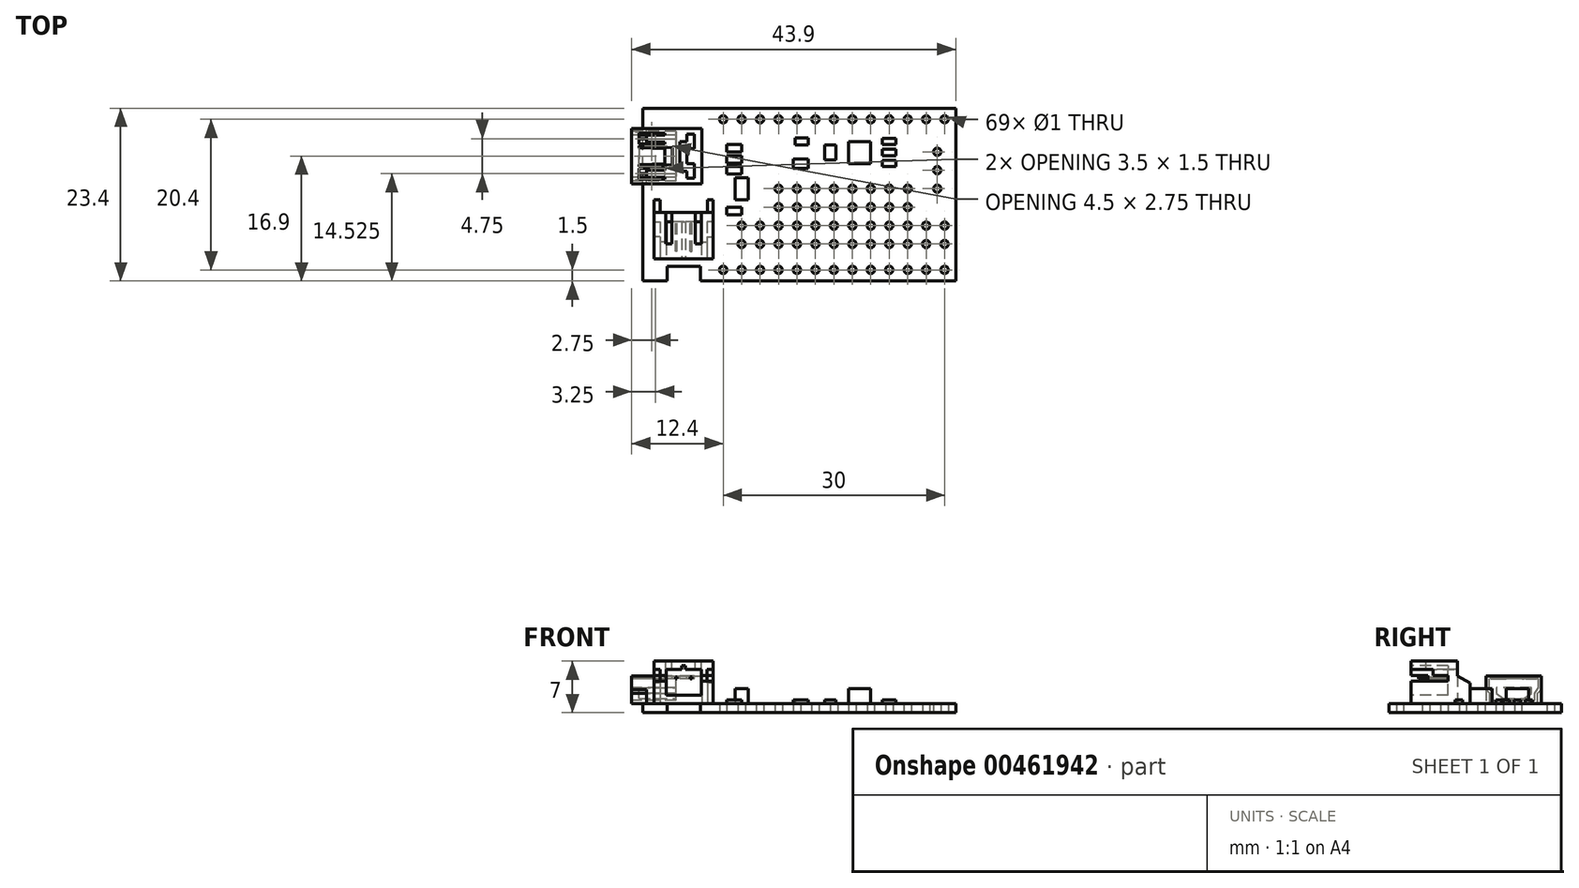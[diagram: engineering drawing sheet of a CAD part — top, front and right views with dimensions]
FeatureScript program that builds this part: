
annotation { "Feature Type Name" : "Feature", "Feature Type Description" : "" }
export const myFeature = defineFeature(function(context is Context, id is Id, definition is map)
    precondition{}
    {
        {
            var Q0;
            Q0=qCreatedBy(makeId("Top.planeOp"),FACE);
            var sketch = newSketch(context, id + "F0", { "sketchPlane" : qUnion([Q0])});
            skLineSegment(sketch, "E0.bottom", {"start": v(21.2, -11.7) * mm, "end": v(-21.2, -11.7) * mm});
            skLineSegment(sketch, "E0.top", {"start": v(21.2, 11.7) * mm, "end": v(-21.2, 11.7) * mm});
            skLineSegment(sketch, "E0.left", {"start": v(21.2, -11.7) * mm, "end": v(21.2, 11.7) * mm});
            skLineSegment(sketch, "E0.right", {"start": v(-21.2, -11.7) * mm, "end": v(-21.2, 11.7) * mm});
            skPoint(sketch, "E0.middle", {"position": v(0, 0) * mm});
            skLineSegment(sketch, "E1.bottom", {"start": v(-17.9, -11.7) * mm, "end": v(-13.4, -11.7) * mm, "construction": true});
            skLineSegment(sketch, "E1.top", {"start": v(-17.9, -9.7) * mm, "end": v(-13.4, -9.7) * mm});
            skLineSegment(sketch, "E1.left", {"start": v(-17.9, -11.7) * mm, "end": v(-17.9, -9.7) * mm});
            skLineSegment(sketch, "E1.right", {"start": v(-13.4, -11.7) * mm, "end": v(-13.4, -9.7) * mm});
            skCircle(sketch, "E2", {"center": v(19.7, -10.2) * mm, "radius": 0.5 * mm});
            skCircle(sketch, "E3.1.0.0", {"center": v(17.2, -10.2) * mm, "radius": 0.5 * mm});
            skCircle(sketch, "E3.2.0.0", {"center": v(14.7, -10.2) * mm, "radius": 0.5 * mm});
            skCircle(sketch, "E3.3.0.0", {"center": v(12.2, -10.2) * mm, "radius": 0.5 * mm});
            skCircle(sketch, "E3.4.0.0", {"center": v(9.7, -10.2) * mm, "radius": 0.5 * mm});
            skCircle(sketch, "E3.5.0.0", {"center": v(7.2, -10.2) * mm, "radius": 0.5 * mm});
            skCircle(sketch, "E3.6.0.0", {"center": v(4.7, -10.2) * mm, "radius": 0.5 * mm});
            skCircle(sketch, "E3.7.0.0", {"center": v(2.2, -10.2) * mm, "radius": 0.5 * mm});
            skCircle(sketch, "E3.8.0.0", {"center": v(-0.3, -10.2) * mm, "radius": 0.5 * mm});
            skCircle(sketch, "E3.9.0.0", {"center": v(-2.8, -10.2) * mm, "radius": 0.5 * mm});
            skCircle(sketch, "E3.10.0.0", {"center": v(-5.3, -10.2) * mm, "radius": 0.5 * mm});
            skCircle(sketch, "E3.11.0.0", {"center": v(-7.8, -10.2) * mm, "radius": 0.5 * mm});
            skCircle(sketch, "E3.12.0.0", {"center": v(-10.3, -10.2) * mm, "radius": 0.5 * mm});
            skLineSegment(sketch, "E3.direction1", {"start": v(19.7, -10.2) * mm, "end": v(17.2, -10.2) * mm, "construction": true});
            skCircle(sketch, "E4.0.1.0", {"center": v(-5.3, -6.7) * mm, "radius": 0.5 * mm});
            skCircle(sketch, "E4.0.1.1", {"center": v(-0.3, -6.7) * mm, "radius": 0.5 * mm});
            skCircle(sketch, "E4.0.1.2", {"center": v(17.2, -6.7) * mm, "radius": 0.5 * mm});
            skCircle(sketch, "E4.0.1.3", {"center": v(14.7, -6.7) * mm, "radius": 0.5 * mm});
            skCircle(sketch, "E4.0.1.4", {"center": v(12.2, -6.7) * mm, "radius": 0.5 * mm});
            skCircle(sketch, "E4.0.1.5", {"center": v(9.7, -6.7) * mm, "radius": 0.5 * mm});
            skCircle(sketch, "E4.0.1.6", {"center": v(19.7, -6.7) * mm, "radius": 0.5 * mm});
            skCircle(sketch, "E4.0.1.7", {"center": v(2.2, -6.7) * mm, "radius": 0.5 * mm});
            skCircle(sketch, "E4.0.1.8", {"center": v(4.7, -6.7) * mm, "radius": 0.5 * mm});
            skCircle(sketch, "E4.0.1.9", {"center": v(7.2, -6.7) * mm, "radius": 0.5 * mm});
            skCircle(sketch, "E4.0.1.10", {"center": v(-2.8, -6.7) * mm, "radius": 0.5 * mm});
            skCircle(sketch, "E4.0.1.12", {"center": v(-7.8, -6.7) * mm, "radius": 0.5 * mm});
            skLineSegment(sketch, "E4.direction1", {"start": v(-7.8, -10.2) * mm, "end": v(17.6, -10.2) * mm, "construction": true});
            skLineSegment(sketch, "E4.direction2", {"start": v(-7.8, -10.2) * mm, "end": v(-7.8, -6.7) * mm, "construction": true});
            skLineSegment(sketch, "E5.direction1", {"start": v(-7.8, -6.7) * mm, "end": v(17.6, -6.7) * mm, "construction": true});
            skLineSegment(sketch, "E5.direction2", {"start": v(-7.8, -6.7) * mm, "end": v(-7.8, -4.85) * mm, "construction": true});
            skPoint(sketch, "E6", {"position": v(-7.8, -8.45) * mm});
            skCircle(sketch, "E7.0.1.0", {"center": v(2.2, -4.2) * mm, "radius": 0.5 * mm});
            skCircle(sketch, "E7.0.1.1", {"center": v(9.7, -4.2) * mm, "radius": 0.5 * mm});
            skCircle(sketch, "E7.0.1.2", {"center": v(-5.3, -4.2) * mm, "radius": 0.5 * mm});
            skCircle(sketch, "E7.0.1.3", {"center": v(17.2, -4.2) * mm, "radius": 0.5 * mm});
            skCircle(sketch, "E7.0.1.4", {"center": v(-2.8, -4.2) * mm, "radius": 0.5 * mm});
            skCircle(sketch, "E7.0.1.5", {"center": v(-0.3, -4.2) * mm, "radius": 0.5 * mm});
            skCircle(sketch, "E7.0.1.6", {"center": v(14.7, -4.2) * mm, "radius": 0.5 * mm});
            skCircle(sketch, "E7.0.1.7", {"center": v(4.7, -4.2) * mm, "radius": 0.5 * mm});
            skCircle(sketch, "E7.0.1.8", {"center": v(7.2, -4.2) * mm, "radius": 0.5 * mm});
            skCircle(sketch, "E7.0.1.10", {"center": v(12.2, -4.2) * mm, "radius": 0.5 * mm});
            skCircle(sketch, "E7.0.1.11", {"center": v(19.7, -4.2) * mm, "radius": 0.5 * mm});
            skCircle(sketch, "E7.0.1.12", {"center": v(-7.8, -4.2) * mm, "radius": 0.5 * mm});
            skCircle(sketch, "E7.0.2.0", {"center": v(2.2, -1.7) * mm, "radius": 0.5 * mm});
            skCircle(sketch, "E7.0.2.1", {"center": v(9.7, -1.7) * mm, "radius": 0.5 * mm});
            skCircle(sketch, "E7.0.2.4", {"center": v(-2.8, -1.7) * mm, "radius": 0.5 * mm});
            skCircle(sketch, "E7.0.2.5", {"center": v(-0.3, -1.7) * mm, "radius": 0.5 * mm});
            skCircle(sketch, "E7.0.2.6", {"center": v(14.7, -1.7) * mm, "radius": 0.5 * mm});
            skCircle(sketch, "E7.0.2.7", {"center": v(4.7, -1.7) * mm, "radius": 0.5 * mm});
            skCircle(sketch, "E7.0.2.8", {"center": v(7.2, -1.7) * mm, "radius": 0.5 * mm});
            skCircle(sketch, "E7.0.2.10", {"center": v(12.2, -1.7) * mm, "radius": 0.5 * mm});
            skCircle(sketch, "E7.0.3.0", {"center": v(2.2, 0.8) * mm, "radius": 0.5 * mm});
            skCircle(sketch, "E7.0.3.1", {"center": v(9.7, 0.8) * mm, "radius": 0.5 * mm});
            skCircle(sketch, "E7.0.3.4", {"center": v(-2.8, 0.8) * mm, "radius": 0.5 * mm});
            skCircle(sketch, "E7.0.3.5", {"center": v(-0.3, 0.8) * mm, "radius": 0.5 * mm});
            skCircle(sketch, "E7.0.3.6", {"center": v(14.7, 0.8) * mm, "radius": 0.5 * mm});
            skCircle(sketch, "E7.0.3.7", {"center": v(4.7, 0.8) * mm, "radius": 0.5 * mm});
            skCircle(sketch, "E7.0.3.8", {"center": v(7.2, 0.8) * mm, "radius": 0.5 * mm});
            skCircle(sketch, "E7.0.3.10", {"center": v(12.2, 0.8) * mm, "radius": 0.5 * mm});
            skLineSegment(sketch, "E7.direction2", {"start": v(-7.8, -6.7) * mm, "end": v(-7.8, -4.2) * mm, "construction": true});
            skCircle(sketch, "E8", {"center": v(19.7, 10.2) * mm, "radius": 0.5 * mm});
            skCircle(sketch, "E9.1.0.0", {"center": v(17.2, 10.2) * mm, "radius": 0.5 * mm});
            skCircle(sketch, "E9.2.0.0", {"center": v(14.7, 10.2) * mm, "radius": 0.5 * mm});
            skCircle(sketch, "E9.3.0.0", {"center": v(12.2, 10.2) * mm, "radius": 0.5 * mm});
            skCircle(sketch, "E9.4.0.0", {"center": v(9.7, 10.2) * mm, "radius": 0.5 * mm});
            skCircle(sketch, "E9.5.0.0", {"center": v(7.2, 10.2) * mm, "radius": 0.5 * mm});
            skCircle(sketch, "E9.6.0.0", {"center": v(4.7, 10.2) * mm, "radius": 0.5 * mm});
            skCircle(sketch, "E9.7.0.0", {"center": v(2.2, 10.2) * mm, "radius": 0.5 * mm});
            skCircle(sketch, "E9.8.0.0", {"center": v(-0.3, 10.2) * mm, "radius": 0.5 * mm});
            skCircle(sketch, "E9.9.0.0", {"center": v(-2.8, 10.2) * mm, "radius": 0.5 * mm});
            skCircle(sketch, "E9.10.0.0", {"center": v(-5.3, 10.2) * mm, "radius": 0.5 * mm});
            skCircle(sketch, "E9.11.0.0", {"center": v(-7.8, 10.2) * mm, "radius": 0.5 * mm});
            skCircle(sketch, "E9.12.0.0", {"center": v(-10.3, 10.2) * mm, "radius": 0.5 * mm});
            skLineSegment(sketch, "E9.direction1", {"start": v(19.7, 10.2) * mm, "end": v(17.2, 10.2) * mm, "construction": true});
            skCircle(sketch, "E10", {"center": v(18.7, 0.8) * mm, "radius": 0.5 * mm});
            skCircle(sketch, "E11.0.1.0", {"center": v(18.7, 3.3) * mm, "radius": 0.5 * mm});
            skCircle(sketch, "E11.0.2.0", {"center": v(18.7, 5.8) * mm, "radius": 0.5 * mm});
            skLineSegment(sketch, "E11.direction1", {"start": v(18.7, 0.8) * mm, "end": v(43.86, 0.8) * mm, "construction": true});
            skLineSegment(sketch, "E11.direction2", {"start": v(18.7, 0.8) * mm, "end": v(18.7, 3.3) * mm, "construction": true});
            skSolve(sketch);
        }
        {
            var Q0;
            Q0=makeQuery(id+"F0.imprint","IMPRINT",FACE,{"disambiguationData":[TD([[makeQuery(id+"F0.imprint","IMPRINT",EDGE,{"derivedFrom":sQuery(id+"F0.wireOp",EDGE,"E0.top")}),1.0]])]});
            extrude(context, id + "F1", {"entities" : qUnion([Q0]), "depth" : 1.25 * mm});
        }
        {
            var Q0;
            Q0=makeQuery(id+"F1.opExtrude","CAP_FACE",FACE,{"disambiguationData":[OSD([sQuery(id+"F0.wireOp",EDGE,"E0.bottom"),sQuery(id+"F0.wireOp",EDGE,"E0.top"),sQuery(id+"F0.wireOp",EDGE,"E0.left"),sQuery(id+"F0.wireOp",EDGE,"E0.right"),sQuery(id+"F0.wireOp",EDGE,"E1.top"),sQuery(id+"F0.wireOp",EDGE,"E1.left"),sQuery(id+"F0.wireOp",EDGE,"E1.right"),sQuery(id+"F0.wireOp",EDGE,"E2"),sQuery(id+"F0.wireOp",EDGE,"E3.1.0.0"),sQuery(id+"F0.wireOp",EDGE,"E3.2.0.0"),sQuery(id+"F0.wireOp",EDGE,"E3.3.0.0"),sQuery(id+"F0.wireOp",EDGE,"E3.4.0.0"),sQuery(id+"F0.wireOp",EDGE,"E3.5.0.0"),sQuery(id+"F0.wireOp",EDGE,"E3.6.0.0"),sQuery(id+"F0.wireOp",EDGE,"E3.7.0.0"),sQuery(id+"F0.wireOp",EDGE,"E3.8.0.0"),sQuery(id+"F0.wireOp",EDGE,"E3.9.0.0"),sQuery(id+"F0.wireOp",EDGE,"E3.10.0.0"),sQuery(id+"F0.wireOp",EDGE,"E3.11.0.0"),sQuery(id+"F0.wireOp",EDGE,"E3.12.0.0"),sQuery(id+"F0.wireOp",EDGE,"E4.0.1.0"),sQuery(id+"F0.wireOp",EDGE,"E4.0.1.1"),sQuery(id+"F0.wireOp",EDGE,"E4.0.1.2"),sQuery(id+"F0.wireOp",EDGE,"E4.0.1.3"),sQuery(id+"F0.wireOp",EDGE,"E4.0.1.4"),sQuery(id+"F0.wireOp",EDGE,"E4.0.1.5"),sQuery(id+"F0.wireOp",EDGE,"E4.0.1.6"),sQuery(id+"F0.wireOp",EDGE,"E4.0.1.7"),sQuery(id+"F0.wireOp",EDGE,"E4.0.1.8"),sQuery(id+"F0.wireOp",EDGE,"E4.0.1.9"),sQuery(id+"F0.wireOp",EDGE,"E4.0.1.10"),sQuery(id+"F0.wireOp",EDGE,"E4.0.1.12"),sQuery(id+"F0.wireOp",EDGE,"E7.0.1.0"),sQuery(id+"F0.wireOp",EDGE,"E7.0.1.1"),sQuery(id+"F0.wireOp",EDGE,"E7.0.1.2"),sQuery(id+"F0.wireOp",EDGE,"E7.0.1.3"),sQuery(id+"F0.wireOp",EDGE,"E7.0.1.4"),sQuery(id+"F0.wireOp",EDGE,"E7.0.1.5"),sQuery(id+"F0.wireOp",EDGE,"E7.0.1.6"),sQuery(id+"F0.wireOp",EDGE,"E7.0.1.7"),sQuery(id+"F0.wireOp",EDGE,"E7.0.1.8"),sQuery(id+"F0.wireOp",EDGE,"E7.0.1.10"),sQuery(id+"F0.wireOp",EDGE,"E7.0.1.11"),sQuery(id+"F0.wireOp",EDGE,"E7.0.1.12"),sQuery(id+"F0.wireOp",EDGE,"E7.0.2.0"),sQuery(id+"F0.wireOp",EDGE,"E7.0.2.1"),sQuery(id+"F0.wireOp",EDGE,"E7.0.2.4"),sQuery(id+"F0.wireOp",EDGE,"E7.0.2.5"),sQuery(id+"F0.wireOp",EDGE,"E7.0.2.6"),sQuery(id+"F0.wireOp",EDGE,"E7.0.2.7"),sQuery(id+"F0.wireOp",EDGE,"E7.0.2.8"),sQuery(id+"F0.wireOp",EDGE,"E7.0.2.10"),sQuery(id+"F0.wireOp",EDGE,"E7.0.3.0"),sQuery(id+"F0.wireOp",EDGE,"E7.0.3.1"),sQuery(id+"F0.wireOp",EDGE,"E7.0.3.4"),sQuery(id+"F0.wireOp",EDGE,"E7.0.3.5"),sQuery(id+"F0.wireOp",EDGE,"E7.0.3.6"),sQuery(id+"F0.wireOp",EDGE,"E7.0.3.7"),sQuery(id+"F0.wireOp",EDGE,"E7.0.3.8"),sQuery(id+"F0.wireOp",EDGE,"E7.0.3.10"),sQuery(id+"F0.wireOp",EDGE,"E8"),sQuery(id+"F0.wireOp",EDGE,"E9.1.0.0"),sQuery(id+"F0.wireOp",EDGE,"E9.2.0.0"),sQuery(id+"F0.wireOp",EDGE,"E9.3.0.0"),sQuery(id+"F0.wireOp",EDGE,"E9.4.0.0"),sQuery(id+"F0.wireOp",EDGE,"E9.5.0.0"),sQuery(id+"F0.wireOp",EDGE,"E9.6.0.0"),sQuery(id+"F0.wireOp",EDGE,"E9.7.0.0"),sQuery(id+"F0.wireOp",EDGE,"E9.8.0.0"),sQuery(id+"F0.wireOp",EDGE,"E9.9.0.0"),sQuery(id+"F0.wireOp",EDGE,"E9.10.0.0"),sQuery(id+"F0.wireOp",EDGE,"E9.11.0.0"),sQuery(id+"F0.wireOp",EDGE,"E9.12.0.0"),sQuery(id+"F0.wireOp",EDGE,"E10"),sQuery(id+"F0.wireOp",EDGE,"E11.0.1.0"),sQuery(id+"F0.wireOp",EDGE,"E11.0.2.0")])],"isStart":false});
            var sketch = newSketch(context, id + "F2", { "sketchPlane" : qUnion([Q0])});
            skCircle(sketch, "E12", {"center": v(12.2, 10.2) * mm, "radius": 0.5 * mm});
            skCircle(sketch, "E13", {"center": v(-7.8, 10.2) * mm, "radius": 0.5 * mm});
            skCircle(sketch, "E14", {"center": v(-2.8, 0.8) * mm, "radius": 0.5 * mm});
            skSolve(sketch);
        }
        {
            var Q0;
            Q0=makeQuery(id+"F1.opExtrude","CAP_FACE",FACE,{"disambiguationData":[OSD([sQuery(id+"F0.wireOp",EDGE,"E0.bottom"),sQuery(id+"F0.wireOp",EDGE,"E0.top"),sQuery(id+"F0.wireOp",EDGE,"E0.left"),sQuery(id+"F0.wireOp",EDGE,"E0.right"),sQuery(id+"F0.wireOp",EDGE,"E1.top"),sQuery(id+"F0.wireOp",EDGE,"E1.left"),sQuery(id+"F0.wireOp",EDGE,"E1.right"),sQuery(id+"F0.wireOp",EDGE,"E2"),sQuery(id+"F0.wireOp",EDGE,"E3.1.0.0"),sQuery(id+"F0.wireOp",EDGE,"E3.2.0.0"),sQuery(id+"F0.wireOp",EDGE,"E3.3.0.0"),sQuery(id+"F0.wireOp",EDGE,"E3.4.0.0"),sQuery(id+"F0.wireOp",EDGE,"E3.5.0.0"),sQuery(id+"F0.wireOp",EDGE,"E3.6.0.0"),sQuery(id+"F0.wireOp",EDGE,"E3.7.0.0"),sQuery(id+"F0.wireOp",EDGE,"E3.8.0.0"),sQuery(id+"F0.wireOp",EDGE,"E3.9.0.0"),sQuery(id+"F0.wireOp",EDGE,"E3.10.0.0"),sQuery(id+"F0.wireOp",EDGE,"E3.11.0.0"),sQuery(id+"F0.wireOp",EDGE,"E3.12.0.0"),sQuery(id+"F0.wireOp",EDGE,"E4.0.1.0"),sQuery(id+"F0.wireOp",EDGE,"E4.0.1.1"),sQuery(id+"F0.wireOp",EDGE,"E4.0.1.2"),sQuery(id+"F0.wireOp",EDGE,"E4.0.1.3"),sQuery(id+"F0.wireOp",EDGE,"E4.0.1.4"),sQuery(id+"F0.wireOp",EDGE,"E4.0.1.5"),sQuery(id+"F0.wireOp",EDGE,"E4.0.1.6"),sQuery(id+"F0.wireOp",EDGE,"E4.0.1.7"),sQuery(id+"F0.wireOp",EDGE,"E4.0.1.8"),sQuery(id+"F0.wireOp",EDGE,"E4.0.1.9"),sQuery(id+"F0.wireOp",EDGE,"E4.0.1.10"),sQuery(id+"F0.wireOp",EDGE,"E4.0.1.12"),sQuery(id+"F0.wireOp",EDGE,"E7.0.1.0"),sQuery(id+"F0.wireOp",EDGE,"E7.0.1.1"),sQuery(id+"F0.wireOp",EDGE,"E7.0.1.2"),sQuery(id+"F0.wireOp",EDGE,"E7.0.1.3"),sQuery(id+"F0.wireOp",EDGE,"E7.0.1.4"),sQuery(id+"F0.wireOp",EDGE,"E7.0.1.5"),sQuery(id+"F0.wireOp",EDGE,"E7.0.1.6"),sQuery(id+"F0.wireOp",EDGE,"E7.0.1.7"),sQuery(id+"F0.wireOp",EDGE,"E7.0.1.8"),sQuery(id+"F0.wireOp",EDGE,"E7.0.1.10"),sQuery(id+"F0.wireOp",EDGE,"E7.0.1.11"),sQuery(id+"F0.wireOp",EDGE,"E7.0.1.12"),sQuery(id+"F0.wireOp",EDGE,"E7.0.2.0"),sQuery(id+"F0.wireOp",EDGE,"E7.0.2.1"),sQuery(id+"F0.wireOp",EDGE,"E7.0.2.4"),sQuery(id+"F0.wireOp",EDGE,"E7.0.2.5"),sQuery(id+"F0.wireOp",EDGE,"E7.0.2.6"),sQuery(id+"F0.wireOp",EDGE,"E7.0.2.7"),sQuery(id+"F0.wireOp",EDGE,"E7.0.2.8"),sQuery(id+"F0.wireOp",EDGE,"E7.0.2.10"),sQuery(id+"F0.wireOp",EDGE,"E7.0.3.0"),sQuery(id+"F0.wireOp",EDGE,"E7.0.3.1"),sQuery(id+"F0.wireOp",EDGE,"E7.0.3.4"),sQuery(id+"F0.wireOp",EDGE,"E7.0.3.5"),sQuery(id+"F0.wireOp",EDGE,"E7.0.3.6"),sQuery(id+"F0.wireOp",EDGE,"E7.0.3.7"),sQuery(id+"F0.wireOp",EDGE,"E7.0.3.8"),sQuery(id+"F0.wireOp",EDGE,"E7.0.3.10"),sQuery(id+"F0.wireOp",EDGE,"E8"),sQuery(id+"F0.wireOp",EDGE,"E9.1.0.0"),sQuery(id+"F0.wireOp",EDGE,"E9.2.0.0"),sQuery(id+"F0.wireOp",EDGE,"E9.3.0.0"),sQuery(id+"F0.wireOp",EDGE,"E9.4.0.0"),sQuery(id+"F0.wireOp",EDGE,"E9.5.0.0"),sQuery(id+"F0.wireOp",EDGE,"E9.6.0.0"),sQuery(id+"F0.wireOp",EDGE,"E9.7.0.0"),sQuery(id+"F0.wireOp",EDGE,"E9.8.0.0"),sQuery(id+"F0.wireOp",EDGE,"E9.9.0.0"),sQuery(id+"F0.wireOp",EDGE,"E9.10.0.0"),sQuery(id+"F0.wireOp",EDGE,"E9.11.0.0"),sQuery(id+"F0.wireOp",EDGE,"E9.12.0.0"),sQuery(id+"F0.wireOp",EDGE,"E10"),sQuery(id+"F0.wireOp",EDGE,"E11.0.1.0"),sQuery(id+"F0.wireOp",EDGE,"E11.0.2.0")])],"isStart":false});
            var sketch = newSketch(context, id + "F3", { "sketchPlane" : qUnion([Q0])});
            skLineSegment(sketch, "E15.bottom", {"start": v(13.13, 3.77) * mm, "end": v(11.28, 3.77) * mm});
            skLineSegment(sketch, "E15.top", {"start": v(13.13, 4.62) * mm, "end": v(11.28, 4.62) * mm});
            skLineSegment(sketch, "E15.left", {"start": v(13.13, 3.77) * mm, "end": v(13.12, 4.62) * mm});
            skLineSegment(sketch, "E15.right", {"start": v(11.28, 3.77) * mm, "end": v(11.28, 4.62) * mm});
            skPoint(sketch, "E15.middle", {"position": v(12.2, 4.2) * mm});
            skPoint(sketch, "E16.0.1.0", {"position": v(12.2, 5.7) * mm});
            skLineSegment(sketch, "E16.0.1.1", {"start": v(13.12, 5.27) * mm, "end": v(11.28, 5.27) * mm});
            skLineSegment(sketch, "E16.0.1.2", {"start": v(13.12, 6.12) * mm, "end": v(11.28, 6.12) * mm});
            skLineSegment(sketch, "E16.0.1.3", {"start": v(13.12, 5.27) * mm, "end": v(13.12, 6.12) * mm});
            skLineSegment(sketch, "E16.0.1.4", {"start": v(11.27, 5.27) * mm, "end": v(11.27, 6.12) * mm});
            skPoint(sketch, "E16.0.2.0", {"position": v(12.2, 7.2) * mm});
            skLineSegment(sketch, "E16.0.2.1", {"start": v(13.13, 6.77) * mm, "end": v(11.28, 6.77) * mm});
            skLineSegment(sketch, "E16.0.2.2", {"start": v(13.13, 7.62) * mm, "end": v(11.28, 7.62) * mm});
            skLineSegment(sketch, "E16.0.2.3", {"start": v(13.12, 6.77) * mm, "end": v(13.12, 7.62) * mm});
            skLineSegment(sketch, "E16.0.2.4", {"start": v(11.27, 6.77) * mm, "end": v(11.27, 7.62) * mm});
            skLineSegment(sketch, "E16.direction1", {"start": v(11.28, 3.77) * mm, "end": v(37.64, 3.77) * mm, "construction": true});
            skLineSegment(sketch, "E16.direction2", {"start": v(11.28, 3.77) * mm, "end": v(11.28, 5.27) * mm, "construction": true});
            skSolve(sketch);
        }
        {
            var Q0;
            Q0=makeQuery(id+"F2.imprint","IMPRINT",FACE,{"disambiguationData":[TD([[makeQuery(id+"F2.imprint","IMPRINT",EDGE,{"derivedFrom":sQuery(id+"F2.wireOp",EDGE,"E12")}),-1.0]])]});
            var sketch = newSketch(context, id + "F4", { "sketchPlane" : qUnion([Q0])});
            skLineSegment(sketch, "E17.bottom", {"start": v(9.7, 4.2) * mm, "end": v(6.7, 4.2) * mm});
            skLineSegment(sketch, "E17.top", {"start": v(9.7, 7.2) * mm, "end": v(6.7, 7.2) * mm});
            skLineSegment(sketch, "E17.left", {"start": v(9.7, 4.2) * mm, "end": v(9.7, 7.2) * mm});
            skLineSegment(sketch, "E17.right", {"start": v(6.7, 4.2) * mm, "end": v(6.7, 7.2) * mm});
            skPoint(sketch, "E17.middle", {"position": v(8.2, 5.7) * mm});
            skSolve(sketch);
        }
        {
            var Q0;
            Q0=makeQuery(id+"F2.imprint","IMPRINT",FACE,{"disambiguationData":[TD([[makeQuery(id+"F2.imprint","IMPRINT",EDGE,{"derivedFrom":sQuery(id+"F2.wireOp",EDGE,"E12")}),-1.0]])]});
            var sketch = newSketch(context, id + "F5", { "sketchPlane" : qUnion([Q0])});
            skLineSegment(sketch, "E18.bottom", {"start": v(4.95, 4.7) * mm, "end": v(3.45, 4.7) * mm});
            skLineSegment(sketch, "E18.top", {"start": v(4.95, 6.7) * mm, "end": v(3.45, 6.7) * mm});
            skLineSegment(sketch, "E18.left", {"start": v(4.95, 4.7) * mm, "end": v(4.95, 6.7) * mm});
            skLineSegment(sketch, "E18.right", {"start": v(3.45, 4.7) * mm, "end": v(3.45, 6.7) * mm});
            skPoint(sketch, "E18.middle", {"position": v(4.2, 5.7) * mm});
            skSolve(sketch);
        }
        {
            var Q0;
            Q0=makeQuery(id+"F2.imprint","IMPRINT",FACE,{"disambiguationData":[TD([[makeQuery(id+"F2.imprint","IMPRINT",EDGE,{"derivedFrom":sQuery(id+"F2.wireOp",EDGE,"E12")}),-1.0]])]});
            var sketch = newSketch(context, id + "F6", { "sketchPlane" : qUnion([Q0])});
            skLineSegment(sketch, "E19.bottom", {"start": v(1.2, 6.7) * mm, "end": v(-0.55, 6.7) * mm});
            skLineSegment(sketch, "E19.top", {"start": v(1.2, 7.7) * mm, "end": v(-0.55, 7.7) * mm});
            skLineSegment(sketch, "E19.left", {"start": v(1.2, 6.7) * mm, "end": v(1.2, 7.7) * mm});
            skLineSegment(sketch, "E19.right", {"start": v(-0.55, 6.7) * mm, "end": v(-0.55, 7.7) * mm});
            skPoint(sketch, "E19.middle", {"position": v(0.32, 7.2) * mm});
            skLineSegment(sketch, "E20.bottom", {"start": v(1.2, 3.57) * mm, "end": v(-0.8, 3.57) * mm});
            skLineSegment(sketch, "E20.top", {"start": v(1.2, 4.82) * mm, "end": v(-0.8, 4.82) * mm});
            skLineSegment(sketch, "E20.left", {"start": v(1.2, 3.57) * mm, "end": v(1.2, 4.82) * mm});
            skLineSegment(sketch, "E20.right", {"start": v(-0.8, 3.57) * mm, "end": v(-0.8, 4.82) * mm});
            skPoint(sketch, "E20.middle", {"position": v(0.2, 4.2) * mm});
            skSolve(sketch);
        }
        {
            var Q0;
            Q0=makeQuery(id+"F2.imprint","IMPRINT",FACE,{"disambiguationData":[TD([[makeQuery(id+"F2.imprint","IMPRINT",EDGE,{"derivedFrom":sQuery(id+"F2.wireOp",EDGE,"E12")}),-1.0]])]});
            var sketch = newSketch(context, id + "F7", { "sketchPlane" : qUnion([Q0])});
            skLineSegment(sketch, "E21.bottom", {"start": v(-7.8, 5.77) * mm, "end": v(-9.8, 5.77) * mm});
            skLineSegment(sketch, "E21.top", {"start": v(-7.8, 6.77) * mm, "end": v(-9.8, 6.77) * mm});
            skLineSegment(sketch, "E21.left", {"start": v(-7.8, 5.77) * mm, "end": v(-7.8, 6.77) * mm});
            skLineSegment(sketch, "E21.right", {"start": v(-9.8, 5.77) * mm, "end": v(-9.8, 6.77) * mm});
            skPoint(sketch, "E21.middle", {"position": v(-8.8, 6.27) * mm});
            skLineSegment(sketch, "E22.0.1.0", {"start": v(-7.8, 4.27) * mm, "end": v(-7.8, 5.27) * mm});
            skLineSegment(sketch, "E22.0.1.1", {"start": v(-9.8, 4.27) * mm, "end": v(-9.8, 5.27) * mm});
            skLineSegment(sketch, "E22.0.1.2", {"start": v(-7.8, 4.27) * mm, "end": v(-9.8, 4.27) * mm});
            skLineSegment(sketch, "E22.0.1.3", {"start": v(-7.8, 5.27) * mm, "end": v(-9.8, 5.27) * mm});
            skPoint(sketch, "E22.0.1.4", {"position": v(-8.8, 4.77) * mm});
            skLineSegment(sketch, "E22.0.2.0", {"start": v(-7.8, 2.77) * mm, "end": v(-7.8, 3.77) * mm});
            skLineSegment(sketch, "E22.0.2.1", {"start": v(-9.8, 2.77) * mm, "end": v(-9.8, 3.77) * mm});
            skLineSegment(sketch, "E22.0.2.2", {"start": v(-7.8, 2.77) * mm, "end": v(-9.8, 2.77) * mm});
            skLineSegment(sketch, "E22.0.2.3", {"start": v(-7.8, 3.77) * mm, "end": v(-9.8, 3.77) * mm});
            skPoint(sketch, "E22.0.2.4", {"position": v(-8.8, 3.27) * mm});
            skLineSegment(sketch, "E22.direction1", {"start": v(-9.8, 5.77) * mm, "end": v(16.86, 5.77) * mm, "construction": true});
            skLineSegment(sketch, "E22.direction2", {"start": v(-9.8, 5.77) * mm, "end": v(-9.8, 4.27) * mm, "construction": true});
            skLineSegment(sketch, "E23.direction1", {"start": v(-9.8, 2.77) * mm, "end": v(15.6, 2.77) * mm, "construction": true});
            skPoint(sketch, "E24.0.1.0", {"position": v(-8.8, -2.23) * mm});
            skLineSegment(sketch, "E24.0.1.1", {"start": v(-9.8, -2.73) * mm, "end": v(-9.8, -1.73) * mm});
            skLineSegment(sketch, "E24.0.1.2", {"start": v(-7.8, -2.73) * mm, "end": v(-7.8, -1.73) * mm});
            skLineSegment(sketch, "E24.0.1.3", {"start": v(-7.8, -1.73) * mm, "end": v(-9.8, -1.73) * mm});
            skLineSegment(sketch, "E24.0.1.4", {"start": v(-7.8, -2.73) * mm, "end": v(-9.8, -2.73) * mm});
            skLineSegment(sketch, "E24.direction2", {"start": v(-9.8, 2.77) * mm, "end": v(-9.8, -2.73) * mm, "construction": true});
            skSolve(sketch);
        }
        {
            var Q0;
            Q0=makeQuery(id+"F2.imprint","IMPRINT",FACE,{"disambiguationData":[TD([[makeQuery(id+"F2.imprint","IMPRINT",EDGE,{"derivedFrom":sQuery(id+"F2.wireOp",EDGE,"E12")}),-1.0]])]});
            var sketch = newSketch(context, id + "F8", { "sketchPlane" : qUnion([Q0])});
            skLineSegment(sketch, "E25.bottom", {"start": v(-6.93, -0.7) * mm, "end": v(-8.68, -0.7) * mm});
            skLineSegment(sketch, "E25.top", {"start": v(-6.93, 2.3) * mm, "end": v(-8.68, 2.3) * mm});
            skLineSegment(sketch, "E25.left", {"start": v(-6.93, -0.7) * mm, "end": v(-6.93, 2.3) * mm});
            skLineSegment(sketch, "E25.right", {"start": v(-8.68, -0.7) * mm, "end": v(-8.68, 2.3) * mm});
            skPoint(sketch, "E25.middle", {"position": v(-7.8, 0.8) * mm});
            skSolve(sketch);
        }
        {
            var Q0;
            Q0 = qSketchRegion(id + "F3", true);
            extrude(context, id + "F9", {"entities" : qUnion([Q0]), "depth" : .5 * mm});
        }
        {
            var Q0;
            Q0 = qSketchRegion(id + "F5", true);
            extrude(context, id + "F10", {"entities" : qUnion([Q0]), "depth" : .5 * mm});
        }
        {
            var Q0;
            Q0 = qSketchRegion(id + "F6", true);
            extrude(context, id + "F11", {"entities" : qUnion([Q0]), "depth" : .5 * mm});
        }
        {
            var Q0;
            Q0 = qSketchRegion(id + "F7", true);
            extrude(context, id + "F12", {"entities" : qUnion([Q0]), "depth" : .5 * mm});
        }
        {
            var Q0;
            Q0 = qSketchRegion(id + "F4", true);
            extrude(context, id + "F13", {"entities" : qUnion([Q0]), "depth" : 2 * mm});
        }
        {
            var Q0;
            Q0 = qSketchRegion(id + "F8", true);
            extrude(context, id + "F14", {"entities" : qUnion([Q0]), "depth" : 2 * mm});
        }
        {
            var Q0;
            Q0=makeQuery(id+"F2.imprint","IMPRINT",FACE,{"disambiguationData":[TD([[makeQuery(id+"F2.imprint","IMPRINT",EDGE,{"derivedFrom":sQuery(id+"F2.wireOp",EDGE,"E12")}),-1.0]])]});
            var sketch = newSketch(context, id + "F15", { "sketchPlane" : qUnion([Q0])});
            skLineSegment(sketch, "E26.bottom", {"start": v(-11.65, -8.7) * mm, "end": v(-19.65, -8.7) * mm});
            skLineSegment(sketch, "E26.top", {"start": v(-11.65, -0.7) * mm, "end": v(-19.65, -0.7) * mm});
            skLineSegment(sketch, "E26.left", {"start": v(-11.65, -8.7) * mm, "end": v(-11.65, -0.7) * mm});
            skLineSegment(sketch, "E26.right", {"start": v(-19.65, -8.7) * mm, "end": v(-19.65, -0.7) * mm});
            skPoint(sketch, "E26.middle", {"position": v(-15.65, -4.7) * mm});
            skLineSegment(sketch, "E27.bottom", {"start": v(-18.85, -0.7) * mm, "end": v(-12.45, -0.7) * mm});
            skLineSegment(sketch, "E27.top", {"start": v(-18.85, -2.45) * mm, "end": v(-12.45, -2.45) * mm});
            skLineSegment(sketch, "E27.left", {"start": v(-18.85, -0.7) * mm, "end": v(-18.85, -2.45) * mm});
            skLineSegment(sketch, "E27.right", {"start": v(-12.45, -0.7) * mm, "end": v(-12.45, -2.45) * mm});
            skPoint(sketch, "E28", {"position": v(-15.65, -2.45) * mm});
            skSolve(sketch);
        }
        {
            var Q0;
            Q0=makeQuery(id+"F15.imprint","IMPRINT",FACE,{"disambiguationData":[TD([[makeQuery(id+"F15.imprint","IMPRINT",EDGE,{"derivedFrom":sQuery(id+"F15.wireOp",EDGE,"E26.bottom")}),-1.0]])]});
            extrude(context, id + "F16", {"entities" : qUnion([Q0]), "depth" : 5.75 * mm});
        }
        {
            var Q0;
            Q0=makeQuery(id+"F2.imprint","IMPRINT",FACE,{"disambiguationData":[TD([[makeQuery(id+"F2.imprint","IMPRINT",EDGE,{"derivedFrom":sQuery(id+"F2.wireOp",EDGE,"E12")}),-1.0]])]});
            var sketch = newSketch(context, id + "F17", { "sketchPlane" : qUnion([Q0])});
            skLineSegment(sketch, "E29.bottom", {"start": v(-22.7, 1.45) * mm, "end": v(-13.2, 1.45) * mm});
            skLineSegment(sketch, "E29.top", {"start": v(-22.7, 8.95) * mm, "end": v(-13.2, 8.95) * mm});
            skLineSegment(sketch, "E29.left", {"start": v(-22.7, 1.45) * mm, "end": v(-22.7, 8.95) * mm});
            skLineSegment(sketch, "E29.right", {"start": v(-13.2, 1.45) * mm, "end": v(-13.2, 8.95) * mm});
            skPoint(sketch, "E29.middle", {"position": v(-17.95, 5.2) * mm});
            skSolve(sketch);
        }
        {
            var Q0;
            Q0 = qSketchRegion(id + "F17", true);
            extrude(context, id + "F18", {"entities" : qUnion([Q0]), "depth" : 3.75 * mm});
        }
        {
            var Q0;
            Q0=makeQuery(id+"F16.opExtrude","SWEPT_FACE",FACE,{"disambiguationData":[OSD([sQuery(id+"F15.wireOp",EDGE,"E26.bottom")])]});
            var sketch = newSketch(context, id + "F19", { "sketchPlane" : qUnion([Q0])});
            skLineSegment(sketch, "E30.bottom", {"start": v(-13.28, 2.37) * mm, "end": v(-18.03, 2.37) * mm});
            skLineSegment(sketch, "E30.top", {"start": v(-13.28, 5.87) * mm, "end": v(-18.03, 5.87) * mm});
            skLineSegment(sketch, "E30.left", {"start": v(-13.28, 2.37) * mm, "end": v(-13.28, 5.87) * mm});
            skLineSegment(sketch, "E30.right", {"start": v(-18.03, 2.37) * mm, "end": v(-18.03, 5.88) * mm});
            skPoint(sketch, "E30.middle", {"position": v(-15.65, 4.12) * mm});
            skSolve(sketch);
        }
        {
            var Q0;
            Q0=makeQuery(id+"F19.imprint","IMPRINT",FACE,{"disambiguationData":[TD([[makeQuery(id+"F19.imprint","IMPRINT",EDGE,{"derivedFrom":sQuery(id+"F19.wireOp",EDGE,"E30.bottom")}),-1.0]])]});
            extrude(context, id + "F20", {"entities" : qUnion([Q0]), "operationType" : NewBodyOperationType.REMOVE, "oppositeDirection" : true, "depth" : 5 * mm});
        }
        {
            var Q0;
            Q0=makeQuery(id+"F18.opExtrude","SWEPT_FACE",FACE,{"disambiguationData":[OSD([sQuery(id+"F17.wireOp",EDGE,"E29.left")])]});
            var sketch = newSketch(context, id + "F21", { "sketchPlane" : qUnion([Q0])});
            skLineSegment(sketch, "E31.bottom", {"start": v(-1.95, 1.25) * mm, "end": v(-8.45, 1.25) * mm});
            skLineSegment(sketch, "E31.top", {"start": v(-1.95, 2.62) * mm, "end": v(-8.45, 2.62) * mm});
            skLineSegment(sketch, "E31.left", {"start": v(-1.95, 1.25) * mm, "end": v(-1.95, 2.62) * mm});
            skLineSegment(sketch, "E31.right", {"start": v(-8.45, 1.25) * mm, "end": v(-8.45, 2.62) * mm});
            skPoint(sketch, "E31.middle", {"position": v(-5.2, 1.94) * mm});
            skLineSegment(sketch, "E32", {"start": v(-8.45, 2.62) * mm, "end": v(-8.95, 3.13) * mm});
            skLineSegment(sketch, "E33", {"start": v(-1.45, 3.12) * mm, "end": v(-1.95, 2.62) * mm});
            skSolve(sketch);
        }
        {
            var Q0;
            {var subQ0=sQuery(id+"F21.wireOp",EDGE,"E31.right");Q0=makeQuery(id+"F21.imprint","IMPRINT",FACE,{"disambiguationData":[TD([[makeQuery(id+"F21.imprint","IMPRINT",EDGE,{"derivedFrom":subQ0}),1.0]])]});}
            var Q1;
            {var subQ0=sQuery(id+"F21.wireOp",EDGE,"E31.left");Q1=makeQuery(id+"F21.imprint","IMPRINT",FACE,{"disambiguationData":[TD([[makeQuery(id+"F21.imprint","IMPRINT",EDGE,{"derivedFrom":subQ0}),-1.0]])]});}
            extrude(context, id + "F22", {"entities" : qUnion([Q0, Q1]), "operationType" : NewBodyOperationType.REMOVE, "oppositeDirection" : true, "depth" : 2 * mm});
        }
        {
            var Q0;
            Q0=makeQuery(id+"F18.opExtrude","SWEPT_FACE",FACE,{"disambiguationData":[OSD([sQuery(id+"F17.wireOp",EDGE,"E29.left")])]});
            var sketch = newSketch(context, id + "F23", { "sketchPlane" : qUnion([Q0])});
            skLineSegment(sketch, "E34", {"start": v(-8.55, 4.6) * mm, "end": v(-1.85, 4.6) * mm});
            skLineSegment(sketch, "E35", {"start": v(-1.85, 4.6) * mm, "end": v(-1.85, 3.37) * mm});
            skLineSegment(sketch, "E36", {"start": v(-1.85, 3.37) * mm, "end": v(-2.35, 2.62) * mm});
            skLineSegment(sketch, "E37", {"start": v(-2.35, 2.62) * mm, "end": v(-2.35, 1.65) * mm});
            skLineSegment(sketch, "E38", {"start": v(-2.35, 1.65) * mm, "end": v(-8.05, 1.65) * mm});
            skLineSegment(sketch, "E39", {"start": v(-8.05, 1.65) * mm, "end": v(-8.05, 2.62) * mm});
            skLineSegment(sketch, "E40", {"start": v(-8.05, 2.62) * mm, "end": v(-8.55, 3.37) * mm});
            skLineSegment(sketch, "E41", {"start": v(-8.55, 3.37) * mm, "end": v(-8.55, 4.6) * mm});
            skPoint(sketch, "E42", {"position": v(-5.2, 4.6) * mm});
            skPoint(sketch, "E43", {"position": v(-5.2, 1.65) * mm});
            skSolve(sketch);
        }
        {
            var Q0;
            Q0=makeQuery(id+"F23.imprint","IMPRINT",FACE,{"disambiguationData":[TD([[makeQuery(id+"F23.imprint","IMPRINT",EDGE,{"derivedFrom":sQuery(id+"F23.wireOp",EDGE,"E34")}),-1.0]])]});
            extrude(context, id + "F24", {"entities" : qUnion([Q0]), "operationType" : NewBodyOperationType.REMOVE, "oppositeDirection" : true, "depth" : 6 * mm});
        }
        {
            var Q0;
            Q0=makeQuery(id+"F18.opExtrude","CAP_FACE",FACE,{"disambiguationData":[OSD([sQuery(id+"F17.wireOp",EDGE,"E29.bottom"),sQuery(id+"F17.wireOp",EDGE,"E29.top"),sQuery(id+"F17.wireOp",EDGE,"E29.left"),sQuery(id+"F17.wireOp",EDGE,"E29.right")])],"isStart":false});
            var sketch = newSketch(context, id + "F25", { "sketchPlane" : qUnion([Q0])});
            skLineSegment(sketch, "E44", {"start": v(-13.2, 5.2) * mm, "end": v(-22.7, 5.2) * mm, "construction": true});
            skLineSegment(sketch, "E45", {"start": v(-17.2, 5.2) * mm, "end": v(-17.2, 6.32) * mm});
            skLineSegment(sketch, "E46", {"start": v(-17.2, 6.32) * mm, "end": v(-21.7, 6.57) * mm});
            skLineSegment(sketch, "E47", {"start": v(-21.7, 6.57) * mm, "end": v(-21.7, 6.32) * mm});
            skLineSegment(sketch, "E48", {"start": v(-21.7, 6.32) * mm, "end": v(-18.2, 6.2) * mm});
            skLineSegment(sketch, "E49", {"start": v(-18.2, 6.2) * mm, "end": v(-18.2, 5.2) * mm});
            skLineSegment(sketch, "E50", {"start": v(-18.2, 8.32) * mm, "end": v(-21.7, 8.32) * mm});
            skLineSegment(sketch, "E51", {"start": v(-21.7, 8.32) * mm, "end": v(-21.7, 6.82) * mm});
            skLineSegment(sketch, "E52", {"start": v(-21.7, 6.82) * mm, "end": v(-18.2, 6.82) * mm});
            skLineSegment(sketch, "E53", {"start": v(-18.2, 6.82) * mm, "end": v(-18.2, 7.07) * mm});
            skLineSegment(sketch, "E54", {"start": v(-18.2, 7.07) * mm, "end": v(-20.7, 7.07) * mm});
            skLineSegment(sketch, "E55", {"start": v(-20.7, 7.07) * mm, "end": v(-20.7, 8.07) * mm});
            skLineSegment(sketch, "E56", {"start": v(-20.7, 8.07) * mm, "end": v(-18.2, 8.07) * mm});
            skLineSegment(sketch, "E57", {"start": v(-18.2, 8.07) * mm, "end": v(-18.2, 8.32) * mm});
            skLineSegment(sketch, "E58", {"start": v(-14.2, 8.2) * mm, "end": v(-14.2, 6.2) * mm});
            skLineSegment(sketch, "E59", {"start": v(-14.2, 6.2) * mm, "end": v(-15.2, 6.2) * mm});
            skLineSegment(sketch, "E60", {"start": v(-15.2, 6.2) * mm, "end": v(-15.2, 5.2) * mm});
            skLineSegment(sketch, "E61", {"start": v(-14.2, 8.2) * mm, "end": v(-15.2, 8.2) * mm});
            skLineSegment(sketch, "E62", {"start": v(-15.2, 8.2) * mm, "end": v(-15.2, 7.2) * mm});
            skLineSegment(sketch, "E63", {"start": v(-15.2, 7.2) * mm, "end": v(-16.2, 7.2) * mm});
            skLineSegment(sketch, "E64", {"start": v(-16.2, 7.2) * mm, "end": v(-16.2, 5.2) * mm});
            skLineSegment(sketch, "E65", {"start": v(-13.2, 8.2) * mm, "end": v(-13.45, 8.2) * mm});
            skLineSegment(sketch, "E66", {"start": v(-13.45, 8.2) * mm, "end": v(-13.45, 5.2) * mm});
            skLineSegment(sketch, "E67.MirrorCS", {"start": v(-21.7, 3.82) * mm, "end": v(-21.7, 4.07) * mm});
            skLineSegment(sketch, "E68.MirrorCS", {"start": v(-18.2, 2.32) * mm, "end": v(-18.2, 2.07) * mm});
            skLineSegment(sketch, "E69.MirrorCS", {"start": v(-18.2, 3.57) * mm, "end": v(-18.2, 3.32) * mm});
            skLineSegment(sketch, "E70.MirrorCS", {"start": v(-13.2, 2.2) * mm, "end": v(-13.45, 2.2) * mm});
            skLineSegment(sketch, "E71.MirrorCS", {"start": v(-17.2, 4.08) * mm, "end": v(-21.7, 3.82) * mm});
            skLineSegment(sketch, "E72.MirrorCS", {"start": v(-17.2, 5.2) * mm, "end": v(-17.2, 4.08) * mm});
            skLineSegment(sketch, "E73.MirrorCS", {"start": v(-21.7, 3.58) * mm, "end": v(-18.2, 3.58) * mm});
            skLineSegment(sketch, "E74.MirrorCS", {"start": v(-18.2, 4.2) * mm, "end": v(-18.2, 5.2) * mm});
            skLineSegment(sketch, "E75.MirrorCS", {"start": v(-14.2, 4.2) * mm, "end": v(-15.2, 4.2) * mm});
            skLineSegment(sketch, "E76.MirrorCS", {"start": v(-21.7, 4.08) * mm, "end": v(-18.2, 4.2) * mm});
            skLineSegment(sketch, "E77.MirrorCS", {"start": v(-14.2, 2.2) * mm, "end": v(-14.2, 4.2) * mm});
            skLineSegment(sketch, "E78.MirrorCS", {"start": v(-15.2, 4.2) * mm, "end": v(-15.2, 5.2) * mm});
            skLineSegment(sketch, "E79.MirrorCS", {"start": v(-15.2, 2.2) * mm, "end": v(-15.2, 3.2) * mm});
            skLineSegment(sketch, "E80.MirrorCS", {"start": v(-18.2, 2.08) * mm, "end": v(-21.7, 2.08) * mm});
            skLineSegment(sketch, "E81.MirrorCS", {"start": v(-20.7, 3.32) * mm, "end": v(-20.7, 2.32) * mm});
            skLineSegment(sketch, "E82.MirrorCS", {"start": v(-15.2, 3.2) * mm, "end": v(-16.2, 3.2) * mm});
            skLineSegment(sketch, "E83.MirrorCS", {"start": v(-21.7, 2.07) * mm, "end": v(-21.7, 3.57) * mm});
            skLineSegment(sketch, "E84.MirrorCS", {"start": v(-20.7, 2.32) * mm, "end": v(-18.2, 2.32) * mm});
            skLineSegment(sketch, "E85.MirrorCS", {"start": v(-18.2, 3.32) * mm, "end": v(-20.7, 3.32) * mm});
            skLineSegment(sketch, "E86.MirrorCS", {"start": v(-14.2, 2.2) * mm, "end": v(-15.2, 2.2) * mm});
            skLineSegment(sketch, "E87.MirrorCS", {"start": v(-16.2, 3.2) * mm, "end": v(-16.2, 5.2) * mm});
            skLineSegment(sketch, "E88.MirrorCS", {"start": v(-13.45, 2.2) * mm, "end": v(-13.45, 5.2) * mm});
            skSolve(sketch);
        }
        {
            var Q0;
            Q0 = qSketchRegion(id + "F25", true);
            var Q1;
            Q1=makeQuery(id+"F24.boolean.opBoolean","COPY",FACE,{"derivedFrom":makeQuery(id+"F24.opExtrude","SWEPT_FACE",FACE,{"disambiguationData":[OSD([sQuery(id+"F23.wireOp",EDGE,"E34")])]})});
            extrude(context, id + "F26", {"entities" : qUnion([Q0]), "operationType" : NewBodyOperationType.REMOVE, "endBound" : BoundingType.UP_TO_SURFACE, "oppositeDirection" : true, "endBoundEntityFace" : qUnion([Q1]), "depth" : 25.4 * mm});
        }
        {
            var Q0;
            Q0=makeQuery(id+"F24.boolean.opBoolean","COPY",FACE,{"derivedFrom":makeQuery(id+"F24.opExtrude","CAP_FACE",FACE,{"disambiguationData":[OSD([sQuery(id+"F23.wireOp",EDGE,"E34"),sQuery(id+"F23.wireOp",EDGE,"E35"),sQuery(id+"F23.wireOp",EDGE,"E36"),sQuery(id+"F23.wireOp",EDGE,"E37"),sQuery(id+"F23.wireOp",EDGE,"E38"),sQuery(id+"F23.wireOp",EDGE,"E39"),sQuery(id+"F23.wireOp",EDGE,"E40"),sQuery(id+"F23.wireOp",EDGE,"E41")])],"isStart":false})});
            var sketch = newSketch(context, id + "F27", { "sketchPlane" : qUnion([Q0])});
            skLineSegment(sketch, "E89", {"start": v(-7.57, 3.4) * mm, "end": v(-2.82, 3.4) * mm});
            skLineSegment(sketch, "E90", {"start": v(-2.82, 3.4) * mm, "end": v(-2.82, 2.65) * mm});
            skLineSegment(sketch, "E91", {"start": v(-2.82, 2.65) * mm, "end": v(-3.82, 1.9) * mm});
            skLineSegment(sketch, "E92", {"start": v(-3.82, 1.9) * mm, "end": v(-6.57, 1.9) * mm});
            skLineSegment(sketch, "E93", {"start": v(-6.57, 1.9) * mm, "end": v(-7.57, 2.65) * mm});
            skLineSegment(sketch, "E94", {"start": v(-7.57, 2.65) * mm, "end": v(-7.57, 3.4) * mm});
            skPoint(sketch, "E95", {"position": v(-5.2, 3.4) * mm});
            skPoint(sketch, "E96", {"position": v(-5.2, 1.9) * mm});
            skSolve(sketch);
        }
        {
            var Q0;
            Q0=makeQuery(id+"F27.imprint","IMPRINT",FACE,{"disambiguationData":[TD([[makeQuery(id+"F27.imprint","IMPRINT",EDGE,{"derivedFrom":sQuery(id+"F27.wireOp",EDGE,"E89")}),-1.0]])]});
            extrude(context, id + "F28", {"entities" : qUnion([Q0]), "depth" : 5 * mm});
        }
        {
            var Q0;
            Q0=makeQuery(id+"F16.opExtrude","CAP_FACE",FACE,{"disambiguationData":[OSD([sQuery(id+"F15.wireOp",EDGE,"E26.bottom"),sQuery(id+"F15.wireOp",EDGE,"E26.top"),sQuery(id+"F15.wireOp",EDGE,"E26.left"),sQuery(id+"F15.wireOp",EDGE,"E26.right"),sQuery(id+"F15.wireOp",EDGE,"E27.top"),sQuery(id+"F15.wireOp",EDGE,"E27.left"),sQuery(id+"F15.wireOp",EDGE,"E27.right")])],"isStart":false});
            var sketch = newSketch(context, id + "F29", { "sketchPlane" : qUnion([Q0])});
            skLineSegment(sketch, "E97", {"start": v(-15.65, -2.45) * mm, "end": v(-15.65, -8.7) * mm, "construction": true});
            skLineSegment(sketch, "E98", {"start": v(-18.05, -2.45) * mm, "end": v(-18.05, -6.7) * mm});
            skLineSegment(sketch, "E99", {"start": v(-18.05, -6.7) * mm, "end": v(-17.25, -6.7) * mm});
            skLineSegment(sketch, "E100", {"start": v(-17.25, -6.7) * mm, "end": v(-17.25, -2.45) * mm});
            skLineSegment(sketch, "E101.MirrorCS", {"start": v(-13.25, -2.45) * mm, "end": v(-13.25, -6.7) * mm});
            skLineSegment(sketch, "E102.MirrorCS", {"start": v(-13.25, -6.7) * mm, "end": v(-14.05, -6.7) * mm});
            skLineSegment(sketch, "E103.MirrorCS", {"start": v(-14.05, -6.7) * mm, "end": v(-14.05, -2.45) * mm});
            skSolve(sketch);
        }
        {
            var Q0;
            {var subQ0=sQuery(id+"F29.wireOp",EDGE,"E98");Q0=makeQuery(id+"F29.imprint","IMPRINT",FACE,{"disambiguationData":[TD([[makeQuery(id+"F29.imprint","IMPRINT",EDGE,{"derivedFrom":subQ0}),1.0]])]});}
            var Q1;
            {var subQ0=sQuery(id+"F29.wireOp",EDGE,"E101.MirrorCS");Q1=makeQuery(id+"F29.imprint","IMPRINT",FACE,{"disambiguationData":[TD([[makeQuery(id+"F29.imprint","IMPRINT",EDGE,{"derivedFrom":subQ0}),-1.0]])]});}
            var Q2;
            Q2=makeQuery(id+"F20.boolean.opBoolean","COPY",FACE,{"derivedFrom":makeQuery(id+"F20.opExtrude","SWEPT_FACE",FACE,{"disambiguationData":[OSD([sQuery(id+"F19.wireOp",EDGE,"E30.top")])]})});
            extrude(context, id + "F30", {"entities" : qUnion([Q0, Q1]), "operationType" : NewBodyOperationType.REMOVE, "endBound" : BoundingType.UP_TO_SURFACE, "oppositeDirection" : true, "endBoundEntityFace" : qUnion([Q2]), "depth" : 25.4 * mm});
        }
        {
            var Q0;
            Q0=makeQuery(id+"F16.opExtrude","SWEPT_FACE",FACE,{"disambiguationData":[OSD([sQuery(id+"F15.wireOp",EDGE,"E26.bottom")])]});
            var sketch = newSketch(context, id + "F31", { "sketchPlane" : qUnion([Q0])});
            skLineSegment(sketch, "E104", {"start": v(-18.03, 5.06) * mm, "end": v(-19.65, 5.06) * mm});
            skLineSegment(sketch, "E105", {"start": v(-18.84, 5.06) * mm, "end": v(-18.84, 4.25) * mm});
            skLineSegment(sketch, "E106", {"start": v(-18.84, 4.25) * mm, "end": v(-18.03, 4.25) * mm});
            skLineSegment(sketch, "E107", {"start": v(-18.84, 4.25) * mm, "end": v(-19.65, 4.25) * mm});
            skLineSegment(sketch, "E108", {"start": v(-18.84, 5.06) * mm, "end": v(-18.84, 5.88) * mm});
            skLineSegment(sketch, "E109", {"start": v(-18.84, 5.88) * mm, "end": v(-19.65, 5.88) * mm});
            skLineSegment(sketch, "E110", {"start": v(-15.65, 7) * mm, "end": v(-15.65, 1.25) * mm, "construction": true});
            skLineSegment(sketch, "E111", {"start": v(-15.9, 5.87) * mm, "end": v(-15.9, 6.37) * mm});
            skLineSegment(sketch, "E112", {"start": v(-15.9, 6.37) * mm, "end": v(-15.65, 6.37) * mm});
            skLineSegment(sketch, "E113.MirrorCS", {"start": v(-15.4, 5.87) * mm, "end": v(-15.4, 6.37) * mm});
            skLineSegment(sketch, "E114.MirrorCS", {"start": v(-12.46, 5.06) * mm, "end": v(-12.46, 4.25) * mm});
            skLineSegment(sketch, "E115.MirrorCS", {"start": v(-13.27, 5.06) * mm, "end": v(-11.65, 5.06) * mm});
            skLineSegment(sketch, "E116.MirrorCS", {"start": v(-12.46, 4.25) * mm, "end": v(-11.65, 4.25) * mm});
            skLineSegment(sketch, "E117.MirrorCS", {"start": v(-15.4, 6.37) * mm, "end": v(-15.65, 6.37) * mm});
            skLineSegment(sketch, "E118.MirrorCS", {"start": v(-12.46, 5.88) * mm, "end": v(-11.65, 5.88) * mm});
            skLineSegment(sketch, "E119.MirrorCS", {"start": v(-12.46, 5.06) * mm, "end": v(-12.46, 5.88) * mm});
            skLineSegment(sketch, "E120.MirrorCS", {"start": v(-12.46, 4.25) * mm, "end": v(-13.27, 4.25) * mm});
            skSolve(sketch);
        }
        {
            var Q0;
            {var subQ1=sQuery(id+"F31.wireOp",EDGE,"E111");Q0=makeQuery(id+"F31.imprint","IMPRINT",FACE,{"disambiguationData":[TD([[makeQuery(id+"F31.imprint","IMPRINT",EDGE,{"derivedFrom":subQ1}),-1.0]])]});}
            var Q1;
            {var subQ3=sQuery(id+"F31.wireOp",EDGE,"E105");Q1=makeQuery(id+"F31.imprint","IMPRINT",FACE,{"disambiguationData":[TD([[makeQuery(id+"F31.imprint","IMPRINT",EDGE,{"derivedFrom":subQ3}),-1.0]])]});}
            var Q2;
            {var subQ0=sQuery(id+"F31.wireOp",EDGE,"E114.MirrorCS");Q2=makeQuery(id+"F31.imprint","IMPRINT",FACE,{"disambiguationData":[TD([[makeQuery(id+"F31.imprint","IMPRINT",EDGE,{"derivedFrom":subQ0}),1.0]])]});}
            var Q3;
            Q3=makeQuery(id+"F20.boolean.opBoolean","COPY",FACE,{"derivedFrom":makeQuery(id+"F20.opExtrude","CAP_FACE",FACE,{"disambiguationData":[OSD([sQuery(id+"F19.wireOp",EDGE,"E30.bottom"),sQuery(id+"F19.wireOp",EDGE,"E30.top"),sQuery(id+"F19.wireOp",EDGE,"E30.left"),sQuery(id+"F19.wireOp",EDGE,"E30.right")])],"isStart":false})});
            extrude(context, id + "F32", {"entities" : qUnion([Q0, Q1, Q2]), "operationType" : NewBodyOperationType.REMOVE, "endBound" : BoundingType.UP_TO_SURFACE, "oppositeDirection" : true, "endBoundEntityFace" : qUnion([Q3]), "depth" : 25.4 * mm});
        }
        {
            var Q0;
            {var subQ3=sQuery(id+"F31.wireOp",EDGE,"E105");Q0=makeQuery(id+"F31.imprint","IMPRINT",FACE,{"disambiguationData":[TD([[makeQuery(id+"F31.imprint","IMPRINT",EDGE,{"derivedFrom":subQ3}),1.0]])]});}
            var Q1;
            {var subQ0=sQuery(id+"F31.wireOp",EDGE,"E114.MirrorCS");Q1=makeQuery(id+"F31.imprint","IMPRINT",FACE,{"disambiguationData":[TD([[makeQuery(id+"F31.imprint","IMPRINT",EDGE,{"derivedFrom":subQ0}),-1.0]])]});}
            extrude(context, id + "F33", {"entities" : qUnion([Q0, Q1]), "operationType" : NewBodyOperationType.REMOVE, "oppositeDirection" : true, "depth" : 2.25 * mm});
        }
        {
            var Q0;
            {var subQ3=sQuery(id+"F31.wireOp",EDGE,"E108");Q0=makeQuery(id+"F31.imprint","IMPRINT",FACE,{"disambiguationData":[TD([[makeQuery(id+"F31.imprint","IMPRINT",EDGE,{"derivedFrom":subQ3}),1.0]])]});}
            var Q1;
            {var subQ4=sQuery(id+"F31.wireOp",EDGE,"E118.MirrorCS");Q1=makeQuery(id+"F31.imprint","IMPRINT",FACE,{"disambiguationData":[TD([[makeQuery(id+"F31.imprint","IMPRINT",EDGE,{"derivedFrom":subQ4}),-1.0]])]});}
            extrude(context, id + "F34", {"entities" : qUnion([Q0, Q1]), "operationType" : NewBodyOperationType.REMOVE, "oppositeDirection" : true, "depth" : 3 * mm});
        }
        {
            var Q0;
            Q0=makeQuery(id+"F16.opExtrude","SWEPT_FACE",FACE,{"disambiguationData":[OSD([sQuery(id+"F15.wireOp",EDGE,"E26.right")])]});
            var sketch = newSketch(context, id + "F35", { "sketchPlane" : qUnion([Q0])});
            skLineSegment(sketch, "E121", {"start": v(2.45, 7) * mm, "end": v(2.45, 5) * mm});
            skLineSegment(sketch, "E122", {"start": v(2.45, 5) * mm, "end": v(0.7, 4) * mm});
            skSolve(sketch);
        }
        {
            var Q0;
            {var subQ0=sQuery(id+"F35.wireOp",EDGE,"E121");Q0=makeQuery(id+"F35.imprint","IMPRINT",FACE,{"disambiguationData":[TD([[makeQuery(id+"F35.imprint","IMPRINT",EDGE,{"derivedFrom":subQ0}),-1.0]])]});}
            extrude(context, id + "F36", {"entities" : qUnion([Q0]), "operationType" : NewBodyOperationType.REMOVE, "endBound" : BoundingType.THROUGH_ALL, "oppositeDirection" : true, "depth" : 25.4 * mm});
        }
        {
            var Q0;
            {var subQ0=sQuery(id+"F19.wireOp",EDGE,"E30.right");var subQ1=sQuery(id+"F19.wireOp",EDGE,"E30.left");var subQ2=sQuery(id+"F19.wireOp",EDGE,"E30.top");var subQ3=sQuery(id+"F19.wireOp",EDGE,"E30.bottom");Q0=makeQuery(id+"F32.boolean.opBoolean","MERGE",FACE,{"derivedFrom":[makeQuery(id+"F20.boolean.opBoolean","COPY",FACE,{"derivedFrom":makeQuery(id+"F20.opExtrude","CAP_FACE",FACE,{"disambiguationData":[OSD([subQ3,subQ2,subQ1,subQ0])],"isStart":false})}),makeQuery(id+"F32.opExtrude","CAP_FACE",FACE,{"disambiguationData":[OSD([subQ3,subQ2,subQ1,subQ0]),ownerDisambiguation([makeQuery(id+"F31.imprint","IMPRINT",EDGE,{"derivedFrom":sQuery(id+"F31.wireOp",EDGE,"E111")})])],"isStart":false})]});}
            var sketch = newSketch(context, id + "F37", { "sketchPlane" : qUnion([Q0])});
            skLineSegment(sketch, "E123", {"start": v(-15.65, 6.37) * mm, "end": v(-15.65, 2.37) * mm, "construction": true});
            skLineSegment(sketch, "E124.bottom", {"start": v(-16.53, 4.62) * mm, "end": v(-16.78, 4.62) * mm});
            skLineSegment(sketch, "E124.top", {"start": v(-16.53, 4.87) * mm, "end": v(-16.78, 4.87) * mm});
            skLineSegment(sketch, "E124.left", {"start": v(-16.53, 4.62) * mm, "end": v(-16.53, 4.87) * mm});
            skLineSegment(sketch, "E124.right", {"start": v(-16.78, 4.62) * mm, "end": v(-16.78, 4.87) * mm});
            skPoint(sketch, "E124.middle", {"position": v(-16.65, 4.75) * mm});
            skPoint(sketch, "E125.MirrorP", {"position": v(-14.65, 4.75) * mm});
            skLineSegment(sketch, "E126.MirrorCS", {"start": v(-14.78, 4.87) * mm, "end": v(-14.53, 4.87) * mm});
            skLineSegment(sketch, "E127.MirrorCS", {"start": v(-14.78, 4.62) * mm, "end": v(-14.53, 4.62) * mm});
            skLineSegment(sketch, "E128.MirrorCS", {"start": v(-14.53, 4.62) * mm, "end": v(-14.53, 4.87) * mm});
            skLineSegment(sketch, "E129.MirrorCS", {"start": v(-14.78, 4.62) * mm, "end": v(-14.78, 4.87) * mm});
            skSolve(sketch);
        }
        {
            var Q0;
            Q0 = qSketchRegion(id + "F37", true);
            var Q1;
            Q1=makeQuery(id+"F33.boolean.opBoolean","COPY",FACE,{"derivedFrom":makeQuery(id+"F33.opExtrude","CAP_FACE",FACE,{"disambiguationData":[OSD([sQuery(id+"F19.wireOp",EDGE,"E30.right"),sQuery(id+"F31.wireOp",EDGE,"E104"),sQuery(id+"F31.wireOp",EDGE,"E105"),sQuery(id+"F31.wireOp",EDGE,"E106")])],"isStart":false})});
            extrude(context, id + "F38", {"entities" : qUnion([Q0]), "endBoundEntityFace" : qUnion([Q1]), "depth" : 4 * mm});
        }
    });
